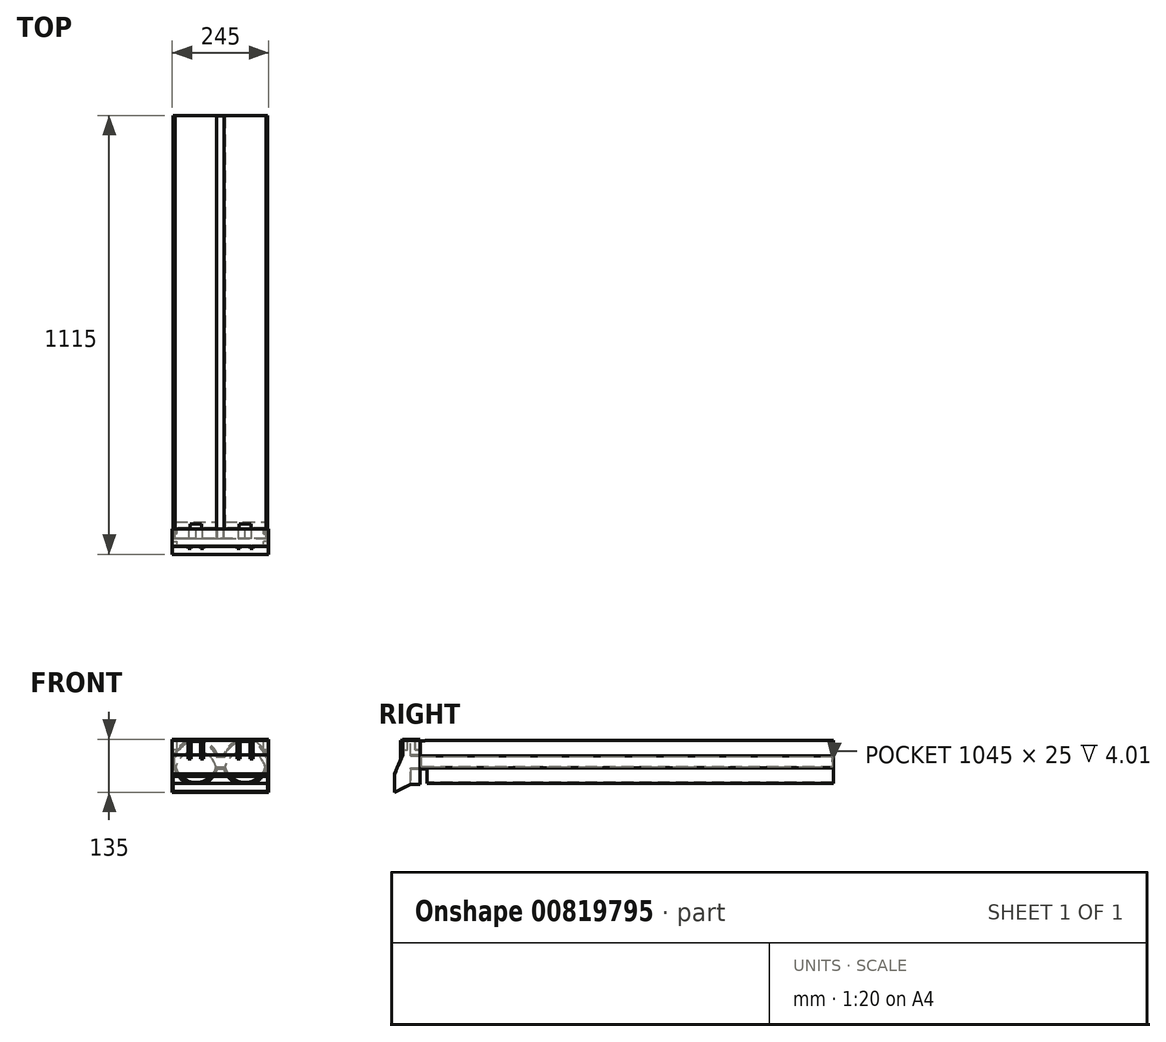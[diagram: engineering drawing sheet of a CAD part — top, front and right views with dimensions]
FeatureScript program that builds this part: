
annotation { "Feature Type Name" : "Feature", "Feature Type Description" : "" }
export const myFeature = defineFeature(function(context is Context, id is Id, definition is map)
    precondition{}
    {
        {
            var Q0;
            Q0=qCreatedBy(makeId("Front.planeOp"),FACE);
            var sketch = newSketch(context, id + "F0", { "sketchPlane" : qUnion([Q0])});
            skLineSegment(sketch, "E0.bottom", {"start": v(-9.58, 15) * mm, "end": v(9.58, 15) * mm});
            skLineSegment(sketch, "E0.top", {"start": v(-9.58, -15) * mm, "end": v(9.58, -15) * mm});
            skLineSegment(sketch, "E0.left", {"start": v(-9.58, 15) * mm, "end": v(-9.58, -15) * mm, "construction": true});
            skLineSegment(sketch, "E0.right", {"start": v(9.58, 15) * mm, "end": v(9.58, -15) * mm, "construction": true});
            skPoint(sketch, "E0.middle", {"position": v(0, 0) * mm});
            skCircle(sketch, "E1", {"center": v(-62.5, 0) * mm, "radius": 55 * mm});
            skCircle(sketch, "E2", {"center": v(62.5, 0) * mm, "radius": 55 * mm});
            skLineSegment(sketch, "E3.bottom", {"start": v(-115.42, 15) * mm, "end": v(-120, 15) * mm});
            skLineSegment(sketch, "E3.top", {"start": v(-115.42, -15) * mm, "end": v(-120, -15) * mm});
            skLineSegment(sketch, "E3.left", {"start": v(-115.42, 15) * mm, "end": v(-115.42, -15) * mm, "construction": true});
            skLineSegment(sketch, "E3.right", {"start": v(-120, 15) * mm, "end": v(-120, -15) * mm});
            skLineSegment(sketch, "E4.bottom", {"start": v(115.42, 15) * mm, "end": v(120, 15) * mm});
            skLineSegment(sketch, "E4.top", {"start": v(115.42, -15) * mm, "end": v(120, -15) * mm});
            skLineSegment(sketch, "E4.left", {"start": v(115.42, 15) * mm, "end": v(115.42, -15) * mm, "construction": true});
            skLineSegment(sketch, "E4.right", {"start": v(120, 15) * mm, "end": v(120, -15) * mm});
            skSolve(sketch);
        }
        {
            var Q0;
            {var subQ0=sQuery(id+"F0.wireOp",EDGE,"E2");var subQ1=makeQuery(id+"F0.imprint","INTERSECT",VERTEX,{"derivedFrom":[sQuery(id+"F0.wireOp",EDGE,"E0.bottom"),subQ0]});Q0=makeQuery(id+"F0.imprint","IMPRINT",FACE,{"disambiguationData":[TD([[makeQuery(id+"F0.imprint","IMPRINT",EDGE,{"disambiguationData":[TD([[subQ1,1.0]])],"derivedFrom":subQ0}),1.0]])]});}
            var Q1;
            {var subQ0=sQuery(id+"F0.wireOp",EDGE,"E4.bottom");Q1=makeQuery(id+"F0.imprint","IMPRINT",FACE,{"disambiguationData":[TD([[makeQuery(id+"F0.imprint","IMPRINT",EDGE,{"derivedFrom":subQ0}),-1.0]])]});}
            var Q2;
            {var subQ0=sQuery(id+"F0.wireOp",EDGE,"E0.bottom");Q2=makeQuery(id+"F0.imprint","IMPRINT",FACE,{"disambiguationData":[TD([[makeQuery(id+"F0.imprint","IMPRINT",EDGE,{"derivedFrom":subQ0}),-1.0]])]});}
            var Q3;
            {var subQ0=sQuery(id+"F0.wireOp",EDGE,"E1");var subQ1=makeQuery(id+"F0.imprint","INTERSECT",VERTEX,{"derivedFrom":[sQuery(id+"F0.wireOp",EDGE,"E0.bottom"),subQ0]});Q3=makeQuery(id+"F0.imprint","IMPRINT",FACE,{"disambiguationData":[TD([[makeQuery(id+"F0.imprint","IMPRINT",EDGE,{"disambiguationData":[TD([[subQ1,-1.0]])],"derivedFrom":subQ0}),1.0]])]});}
            var Q4;
            {var subQ0=sQuery(id+"F0.wireOp",EDGE,"E3.bottom");Q4=makeQuery(id+"F0.imprint","IMPRINT",FACE,{"disambiguationData":[TD([[makeQuery(id+"F0.imprint","IMPRINT",EDGE,{"derivedFrom":subQ0}),1.0]])]});}
            extrude(context, id + "F1", {"entities" : qUnion([Q0, Q1, Q2, Q3, Q4]), "oppositeDirection" : true, "depth" : 1050 * mm, "offsetDistance" : 25 * mm});
        }
        {
            var Q0;
            Q0=makeQuery(id+"F1.opExtrude","CAP_FACE",FACE,{"disambiguationData":[OSD([sQuery(id+"F0.wireOp",EDGE,"E0.bottom"),sQuery(id+"F0.wireOp",EDGE,"E0.top"),sQuery(id+"F0.wireOp",EDGE,"E1"),sQuery(id+"F0.wireOp",EDGE,"E2"),sQuery(id+"F0.wireOp",EDGE,"E3.bottom"),sQuery(id+"F0.wireOp",EDGE,"E3.top"),sQuery(id+"F0.wireOp",EDGE,"E3.right"),sQuery(id+"F0.wireOp",EDGE,"E4.bottom"),sQuery(id+"F0.wireOp",EDGE,"E4.top"),sQuery(id+"F0.wireOp",EDGE,"E4.right")])],"isStart":true});
            shell(context, id + "F2", {"entities" : qUnion([Q0]), "thickness" : 2.5 * mm});
        }
        {
            var Q0;
            Q0=qCreatedBy(makeId("Front.planeOp"),FACE);
            var sketch = newSketch(context, id + "F3", { "sketchPlane" : qUnion([Q0])});
            skLineSegment(sketch, "E5.bottom", {"start": v(122.5, -57.5) * mm, "end": v(-122.5, -57.5) * mm});
            skLineSegment(sketch, "E5.top", {"start": v(122.5, 57.5) * mm, "end": v(-122.5, 57.5) * mm});
            skLineSegment(sketch, "E5.left", {"start": v(122.5, -57.5) * mm, "end": v(122.5, 57.5) * mm});
            skLineSegment(sketch, "E5.right", {"start": v(-122.5, -57.5) * mm, "end": v(-122.5, 57.5) * mm});
            skPoint(sketch, "E5.middle", {"position": v(0, 0) * mm});
            skSolve(sketch);
        }
        {
            var Q0;
            Q0=makeQuery(id+"F3.imprint","IMPRINT",FACE,{"disambiguationData":[TD([[makeQuery(id+"F3.imprint","IMPRINT",EDGE,{"derivedFrom":sQuery(id+"F3.wireOp",EDGE,"E5.bottom")}),-1.0]])]});
            extrude(context, id + "F4", {"entities" : qUnion([Q0]), "depth" : 25 * mm, "offsetDistance" : 25 * mm});
        }
        {
            var Q0;
            {var subQ0=sQuery(id+"F0.wireOp",EDGE,"E3.bottom");Q0=makeQuery(id+"F0.imprint","IMPRINT",FACE,{"disambiguationData":[TD([[makeQuery(id+"F0.imprint","IMPRINT",EDGE,{"derivedFrom":subQ0}),1.0]])]});}
            var Q1;
            {var subQ0=sQuery(id+"F0.wireOp",EDGE,"E1");var subQ1=makeQuery(id+"F0.imprint","INTERSECT",VERTEX,{"derivedFrom":[sQuery(id+"F0.wireOp",EDGE,"E0.bottom"),subQ0]});Q1=makeQuery(id+"F0.imprint","IMPRINT",FACE,{"disambiguationData":[TD([[makeQuery(id+"F0.imprint","IMPRINT",EDGE,{"disambiguationData":[TD([[subQ1,-1.0]])],"derivedFrom":subQ0}),1.0]])]});}
            var Q2;
            {var subQ0=sQuery(id+"F0.wireOp",EDGE,"E0.bottom");Q2=makeQuery(id+"F0.imprint","IMPRINT",FACE,{"disambiguationData":[TD([[makeQuery(id+"F0.imprint","IMPRINT",EDGE,{"derivedFrom":subQ0}),-1.0]])]});}
            var Q3;
            {var subQ0=sQuery(id+"F0.wireOp",EDGE,"E2");var subQ1=makeQuery(id+"F0.imprint","INTERSECT",VERTEX,{"derivedFrom":[sQuery(id+"F0.wireOp",EDGE,"E0.bottom"),subQ0]});Q3=makeQuery(id+"F0.imprint","IMPRINT",FACE,{"disambiguationData":[TD([[makeQuery(id+"F0.imprint","IMPRINT",EDGE,{"disambiguationData":[TD([[subQ1,1.0]])],"derivedFrom":subQ0}),1.0]])]});}
            var Q4;
            {var subQ0=sQuery(id+"F0.wireOp",EDGE,"E4.bottom");Q4=makeQuery(id+"F0.imprint","IMPRINT",FACE,{"disambiguationData":[TD([[makeQuery(id+"F0.imprint","IMPRINT",EDGE,{"derivedFrom":subQ0}),-1.0]])]});}
            extrude(context, id + "F5", {"entities" : qUnion([Q0, Q1, Q2, Q3, Q4]), "operationType" : NewBodyOperationType.REMOVE, "depth" : 25 * mm, "offsetDistance" : 25 * mm});
        }
        {
            var Q0;
            Q0=makeQuery(id+"F1.opExtrude","CAP_FACE",FACE,{"disambiguationData":[OSD([sQuery(id+"F0.wireOp",EDGE,"E0.bottom"),sQuery(id+"F0.wireOp",EDGE,"E0.top"),sQuery(id+"F0.wireOp",EDGE,"E1"),sQuery(id+"F0.wireOp",EDGE,"E2"),sQuery(id+"F0.wireOp",EDGE,"E3.bottom"),sQuery(id+"F0.wireOp",EDGE,"E3.top"),sQuery(id+"F0.wireOp",EDGE,"E3.right"),sQuery(id+"F0.wireOp",EDGE,"E4.bottom"),sQuery(id+"F0.wireOp",EDGE,"E4.top"),sQuery(id+"F0.wireOp",EDGE,"E4.right")])],"isStart":true});
            var sketch = newSketch(context, id + "F6", { "sketchPlane" : qUnion([Q0])});
            skLineSegment(sketch, "E6", {"start": v(-62.5, 52.5) * mm, "end": v(-62.5, -52.5) * mm, "construction": true});
            skLineSegment(sketch, "E7", {"start": v(62.5, 52.5) * mm, "end": v(62.5, -52.5) * mm, "construction": true});
            skLineSegment(sketch, "E8", {"start": v(-120, 0) * mm, "end": v(120, 0) * mm, "construction": true});
            skCircle(sketch, "E9", {"center": v(-62.5, -25) * mm, "radius": 52.5 * mm});
            skCircle(sketch, "E10", {"center": v(62.5, -25) * mm, "radius": 52.5 * mm});
            skSolve(sketch);
        }
        {
            var Q0;
            {var subQ10=sQuery(id+"F0.wireOp",EDGE,"E0.bottom");Q0=makeQuery(id+"F6.imprint","IMPRINT",FACE,{"disambiguationData":[TD([[makeQuery(id+"F6.imprint","IMPRINT",EDGE,{"derivedFrom":makeQuery(id+"F2.opShell","OFFSET_EDGE",EDGE,{"disambiguationData":[OSD([subQ10]),TDD([makeQuery(id+"F1.opExtrude","CAP_EDGE",EDGE,{"disambiguationData":[OSD([subQ10])],"isStart":true})])]})}),-1.0]])]});}
            extrude(context, id + "F7", {"entities" : qUnion([Q0]), "operationType" : NewBodyOperationType.ADD, "oppositeDirection" : true, "depth" : 2.5 * mm, "offsetDistance" : 25 * mm});
        }
        {
            var Q0;
            {var subQ1=sQuery(id+"F0.wireOp",EDGE,"E1");var subQ2=sQuery(id+"F0.wireOp",EDGE,"E0.top");var subQ4=makeQuery(id+"F1.opExtrude","CAP_EDGE",EDGE,{"disambiguationData":[OSD([subQ1]),TDD([makeQuery(id+"F0.imprint","IMPRINT",EDGE,{"disambiguationData":[TD([[makeQuery(id+"F0.imprint","INTERSECT",VERTEX,{"derivedFrom":[subQ2,subQ1]}),1.0]])],"derivedFrom":subQ1})])],"isStart":true});var subQ5=makeQuery(id+"F2.opShell","OFFSET_EDGE",EDGE,{"disambiguationData":[OSD([subQ1]),TDD([subQ4])]});Q0=makeQuery(id+"F6.imprint","IMPRINT",FACE,{"disambiguationData":[TD([[makeQuery(id+"F6.imprint","IMPRINT",EDGE,{"derivedFrom":subQ5}),-1.0]])]});}
            var Q1;
            {var subQ2=sQuery(id+"F0.wireOp",EDGE,"E2");var subQ3=sQuery(id+"F0.wireOp",EDGE,"E0.top");var subQ4=makeQuery(id+"F1.opExtrude","CAP_EDGE",EDGE,{"disambiguationData":[OSD([subQ2]),TDD([makeQuery(id+"F0.imprint","IMPRINT",EDGE,{"disambiguationData":[TD([[makeQuery(id+"F0.imprint","INTERSECT",VERTEX,{"derivedFrom":[subQ3,subQ2]}),-1.0]])],"derivedFrom":subQ2})])],"isStart":true});var subQ5=makeQuery(id+"F2.opShell","OFFSET_EDGE",EDGE,{"disambiguationData":[OSD([subQ2]),TDD([subQ4])]});Q1=makeQuery(id+"F6.imprint","IMPRINT",FACE,{"disambiguationData":[TD([[makeQuery(id+"F6.imprint","IMPRINT",EDGE,{"derivedFrom":subQ5}),-1.0]])]});}
            extrude(context, id + "F8", {"entities" : qUnion([Q0, Q1]), "operationType" : NewBodyOperationType.REMOVE, "oppositeDirection" : true, "depth" : 17.5 * mm, "offsetDistance" : 25 * mm});
        }
        {
            var Q0;
            {var subQ0=sQuery(id+"F0.wireOp",EDGE,"E4.right");var subQ1=sQuery(id+"F0.wireOp",EDGE,"E4.top");var subQ2=sQuery(id+"F0.wireOp",EDGE,"E4.bottom");var subQ3=sQuery(id+"F0.wireOp",EDGE,"E3.right");var subQ4=sQuery(id+"F0.wireOp",EDGE,"E3.top");var subQ5=sQuery(id+"F0.wireOp",EDGE,"E3.bottom");var subQ6=sQuery(id+"F0.wireOp",EDGE,"E2");var subQ7=sQuery(id+"F0.wireOp",EDGE,"E1");var subQ8=sQuery(id+"F0.wireOp",EDGE,"E0.top");var subQ9=sQuery(id+"F0.wireOp",EDGE,"E0.bottom");Q0=makeQuery(id+"F7.boolean.opBoolean","MERGE",FACE,{"derivedFrom":[makeQuery(id+"F1.opExtrude","CAP_FACE",FACE,{"disambiguationData":[OSD([subQ9,subQ8,subQ7,subQ6,subQ5,subQ4,subQ3,subQ2,subQ1,subQ0])],"isStart":true}),makeQuery(id+"F7.opExtrude","CAP_FACE",FACE,{"disambiguationData":[OSD([subQ9,subQ8,subQ7,subQ6,subQ5,subQ4,subQ3,subQ2,subQ1,subQ0,sQuery(id+"F6.wireOp",EDGE,"E9"),sQuery(id+"F6.wireOp",EDGE,"E10")])],"isStart":true})]});}
            var sketch = newSketch(context, id + "F9", { "sketchPlane" : qUnion([Q0])});
            skLineSegment(sketch, "E11", {"start": v(-62.5, 55) * mm, "end": v(-62.5, -55.98) * mm, "construction": true});
            skLineSegment(sketch, "E12", {"start": v(62.5, 55) * mm, "end": v(62.5, -55.98) * mm, "construction": true});
            skLineSegment(sketch, "E13", {"start": v(-77.5, 52.92) * mm, "end": v(-77.5, 25.31) * mm});
            skLineSegment(sketch, "E14", {"start": v(-47.5, 52.92) * mm, "end": v(-47.5, 25.31) * mm});
            skLineSegment(sketch, "E15", {"start": v(47.5, 52.92) * mm, "end": v(47.5, 25.31) * mm});
            skLineSegment(sketch, "E16", {"start": v(77.5, 52.92) * mm, "end": v(77.5, 25.31) * mm});
            skSolve(sketch);
        }
        {
            var Q0;
            {var subQ0=sQuery(id+"F9.wireOp",EDGE,"E13");Q0=makeQuery(id+"F9.imprint","IMPRINT",FACE,{"disambiguationData":[TD([[makeQuery(id+"F9.imprint","IMPRINT",EDGE,{"derivedFrom":subQ0}),1.0]])]});}
            var Q1;
            {var subQ0=sQuery(id+"F9.wireOp",EDGE,"E15");Q1=makeQuery(id+"F9.imprint","IMPRINT",FACE,{"disambiguationData":[TD([[makeQuery(id+"F9.imprint","IMPRINT",EDGE,{"derivedFrom":subQ0}),1.0]])]});}
            extrude(context, id + "F10", {"entities" : qUnion([Q0, Q1]), "operationType" : NewBodyOperationType.REMOVE, "oppositeDirection" : true, "depth" : 12.5 * mm, "offsetDistance" : 25 * mm});
        }
        {
            var Q0;
            Q0=makeQuery(id+"F4.opExtrude","SWEPT_FACE",FACE,{"disambiguationData":[OSD([sQuery(id+"F3.wireOp",EDGE,"E5.right")])]});
            var sketch = newSketch(context, id + "F11", { "sketchPlane" : qUnion([Q0])});
            skLineSegment(sketch, "E17", {"start": v(25, 57.5) * mm, "end": v(45, 57.5) * mm});
            skLineSegment(sketch, "E18", {"start": v(45, 57.5) * mm, "end": v(45, 17.5) * mm});
            skLineSegment(sketch, "E19", {"start": v(45, 17.5) * mm, "end": v(85, -77.5) * mm});
            skLineSegment(sketch, "E20", {"start": v(85, -77.5) * mm, "end": v(65, -77.5) * mm});
            skLineSegment(sketch, "E21", {"start": v(65, -77.5) * mm, "end": v(25, -57.5) * mm});
            skLineSegment(sketch, "E22", {"start": v(65, -77.5) * mm, "end": v(65, -30) * mm});
            skSolve(sketch);
        }
        {
            var Q0;
            Q0=makeQuery(id+"F11.imprint","IMPRINT",FACE,{"disambiguationData":[TD([[makeQuery(id+"F11.imprint","IMPRINT",EDGE,{"derivedFrom":sQuery(id+"F11.wireOp",EDGE,"E17")}),-1.0]])]});
            extrude(context, id + "F12", {"entities" : qUnion([Q0]), "operationType" : NewBodyOperationType.ADD, "oppositeDirection" : true, "depth" : 245 * mm, "offsetDistance" : 25 * mm});
        }
        {
            var Q0;
            Q0=makeQuery(id+"F12.opExtrude","SWEPT_FACE",FACE,{"disambiguationData":[OSD([sQuery(id+"F11.wireOp",EDGE,"E22")])]});
            var Q1;
            Q1=makeQuery(id+"F12.opExtrude","SWEPT_FACE",FACE,{"disambiguationData":[OSD([sQuery(id+"F3.wireOp",EDGE,"E5.right")])]});
            shell(context, id + "F13", {"entities" : qUnion([Q0, Q1]), "thickness" : 2.5 * mm});
        }
        {
            var Q0;
            Q0=makeQuery(id+"F12.opExtrude","SWEPT_FACE",FACE,{"disambiguationData":[OSD([sQuery(id+"F11.wireOp",EDGE,"E18")])]});
            var sketch = newSketch(context, id + "F14", { "sketchPlane" : qUnion([Q0])});
            skLineSegment(sketch, "E23.bottom", {"start": v(-77.5, 57.5) * mm, "end": v(-47.5, 57.5) * mm});
            skLineSegment(sketch, "E23.top", {"start": v(-77.5, 7.5) * mm, "end": v(-47.5, 7.5) * mm});
            skLineSegment(sketch, "E23.left", {"start": v(-77.5, 57.5) * mm, "end": v(-77.5, 7.5) * mm});
            skLineSegment(sketch, "E23.right", {"start": v(-47.5, 57.5) * mm, "end": v(-47.5, 7.5) * mm});
            skLineSegment(sketch, "E24.bottom", {"start": v(47.5, 57.5) * mm, "end": v(77.5, 57.5) * mm});
            skLineSegment(sketch, "E24.top", {"start": v(47.5, 7.5) * mm, "end": v(77.5, 7.5) * mm});
            skLineSegment(sketch, "E24.left", {"start": v(47.5, 57.5) * mm, "end": v(47.5, 7.5) * mm});
            skLineSegment(sketch, "E24.right", {"start": v(77.5, 57.5) * mm, "end": v(77.5, 7.5) * mm});
            skLineSegment(sketch, "E25", {"start": v(-62.5, 57.5) * mm, "end": v(-62.5, 17.5) * mm, "construction": true});
            skLineSegment(sketch, "E26", {"start": v(62.5, 57.5) * mm, "end": v(62.5, 0) * mm, "construction": true});
            skSolve(sketch);
        }
        {
            var Q0;
            Q0=makeQuery(id+"F14.imprint","IMPRINT",FACE,{"disambiguationData":[TD([[makeQuery(id+"F14.imprint","IMPRINT",EDGE,{"derivedFrom":sQuery(id+"F14.wireOp",EDGE,"E23.bottom")}),1.0]])]});
            var Q1;
            Q1=makeQuery(id+"F14.imprint","IMPRINT",FACE,{"disambiguationData":[TD([[makeQuery(id+"F14.imprint","IMPRINT",EDGE,{"derivedFrom":sQuery(id+"F14.wireOp",EDGE,"E24.bottom")}),1.0]])]});
            extrude(context, id + "F15", {"entities" : qUnion([Q0, Q1]), "operationType" : NewBodyOperationType.REMOVE, "oppositeDirection" : true, "depth" : 2.5 * mm, "offsetDistance" : 25 * mm});
        }
        {
            var Q0;
            Q0=makeQuery(id+"F12.boolean.opBoolean","MERGE",FACE,{"derivedFrom":[makeQuery(id+"F4.opExtrude","SWEPT_FACE",FACE,{"disambiguationData":[OSD([sQuery(id+"F3.wireOp",EDGE,"E5.top")])]}),makeQuery(id+"F12.opExtrude","SWEPT_FACE",FACE,{"disambiguationData":[OSD([sQuery(id+"F11.wireOp",EDGE,"E17")])]})]});
            var sketch = newSketch(context, id + "F16", { "sketchPlane" : qUnion([Q0])});
            skLineSegment(sketch, "E27.bottom", {"start": v(-82.5, -45) * mm, "end": v(-80, -45) * mm});
            skLineSegment(sketch, "E27.top", {"start": v(-82.5, -47.5) * mm, "end": v(-80, -47.5) * mm});
            skLineSegment(sketch, "E27.left", {"start": v(-82.5, -45) * mm, "end": v(-82.5, -47.5) * mm});
            skLineSegment(sketch, "E27.right", {"start": v(-80, -45) * mm, "end": v(-80, -47.5) * mm});
            skLineSegment(sketch, "E28.bottom", {"start": v(-82.5, -47.5) * mm, "end": v(-75, -47.5) * mm});
            skLineSegment(sketch, "E28.top", {"start": v(-82.5, -50) * mm, "end": v(-75, -50) * mm});
            skLineSegment(sketch, "E28.left", {"start": v(-82.5, -47.5) * mm, "end": v(-82.5, -50) * mm});
            skLineSegment(sketch, "E28.right", {"start": v(-75, -47.5) * mm, "end": v(-75, -50) * mm});
            skLineSegment(sketch, "E29", {"start": v(-62.5, -42.5) * mm, "end": v(-62.5, -62.36) * mm, "construction": true});
            skLineSegment(sketch, "E30.MirrorCS", {"start": v(-50, -47.5) * mm, "end": v(-50, -50) * mm});
            skLineSegment(sketch, "E31.MirrorCS", {"start": v(-42.5, -47.5) * mm, "end": v(-50, -47.5) * mm});
            skLineSegment(sketch, "E32.MirrorCS", {"start": v(-42.5, -50) * mm, "end": v(-50, -50) * mm});
            skLineSegment(sketch, "E33.MirrorCS", {"start": v(-42.5, -47.5) * mm, "end": v(-42.5, -50) * mm});
            skLineSegment(sketch, "E34.MirrorCS", {"start": v(-42.5, -45) * mm, "end": v(-42.5, -47.5) * mm});
            skLineSegment(sketch, "E35.MirrorCS", {"start": v(-45, -45) * mm, "end": v(-45, -47.5) * mm});
            skLineSegment(sketch, "E36.MirrorCS", {"start": v(-42.5, -45) * mm, "end": v(-45, -45) * mm});
            skLineSegment(sketch, "E37", {"start": v(0, -7.26) * mm, "end": v(0, -62.51) * mm, "construction": true});
            skPoint(sketch, "E37.endSnap0", {"position": v(0, -45) * mm});
            skLineSegment(sketch, "E38.MirrorCS", {"start": v(42.5, -45) * mm, "end": v(42.5, -47.5) * mm});
            skLineSegment(sketch, "E39.MirrorCS", {"start": v(42.5, -45) * mm, "end": v(45, -45) * mm});
            skLineSegment(sketch, "E40.MirrorCS", {"start": v(45, -45) * mm, "end": v(45, -47.5) * mm});
            skLineSegment(sketch, "E41.MirrorCS", {"start": v(42.5, -47.5) * mm, "end": v(50, -47.5) * mm});
            skLineSegment(sketch, "E42.MirrorCS", {"start": v(42.5, -47.5) * mm, "end": v(42.5, -50) * mm});
            skLineSegment(sketch, "E43.MirrorCS", {"start": v(42.5, -50) * mm, "end": v(50, -50) * mm});
            skLineSegment(sketch, "E44.MirrorCS", {"start": v(50, -47.5) * mm, "end": v(50, -50) * mm});
            skLineSegment(sketch, "E45.MirrorCS", {"start": v(82.5, -45) * mm, "end": v(80, -45) * mm});
            skLineSegment(sketch, "E46.MirrorCS", {"start": v(82.5, -45) * mm, "end": v(82.5, -47.5) * mm});
            skLineSegment(sketch, "E47.MirrorCS", {"start": v(80, -45) * mm, "end": v(80, -47.5) * mm});
            skLineSegment(sketch, "E48.MirrorCS", {"start": v(82.5, -47.5) * mm, "end": v(75, -47.5) * mm});
            skLineSegment(sketch, "E49.MirrorCS", {"start": v(82.5, -47.5) * mm, "end": v(82.5, -50) * mm});
            skLineSegment(sketch, "E50.MirrorCS", {"start": v(82.5, -50) * mm, "end": v(75, -50) * mm});
            skLineSegment(sketch, "E51.MirrorCS", {"start": v(75, -47.5) * mm, "end": v(75, -50) * mm});
            skSolve(sketch);
        }
        {
            var Q0;
            Q0=makeQuery(id+"F16.imprint","IMPRINT",FACE,{"disambiguationData":[TD([[makeQuery(id+"F16.imprint","IMPRINT",EDGE,{"derivedFrom":sQuery(id+"F16.wireOp",EDGE,"E27.bottom")}),1.0]])]});
            var Q1;
            Q1=makeQuery(id+"F16.imprint","IMPRINT",FACE,{"disambiguationData":[TD([[makeQuery(id+"F16.imprint","IMPRINT",EDGE,{"derivedFrom":sQuery(id+"F16.wireOp",EDGE,"E28.top")}),1.0]])]});
            var Q2;
            {var subQ0=sQuery(id+"F16.wireOp",EDGE,"E34.MirrorCS");Q2=makeQuery(id+"F16.imprint","IMPRINT",FACE,{"disambiguationData":[TD([[makeQuery(id+"F16.imprint","IMPRINT",EDGE,{"derivedFrom":subQ0}),-1.0]])]});}
            var Q3;
            {var subQ1=sQuery(id+"F16.wireOp",EDGE,"E30.MirrorCS");Q3=makeQuery(id+"F16.imprint","IMPRINT",FACE,{"disambiguationData":[TD([[makeQuery(id+"F16.imprint","IMPRINT",EDGE,{"derivedFrom":subQ1}),1.0]])]});}
            var Q4;
            {var subQ0=sQuery(id+"F16.wireOp",EDGE,"E42.MirrorCS");Q4=makeQuery(id+"F16.imprint","IMPRINT",FACE,{"disambiguationData":[TD([[makeQuery(id+"F16.imprint","IMPRINT",EDGE,{"derivedFrom":subQ0}),1.0]])]});}
            var Q5;
            {var subQ0=sQuery(id+"F16.wireOp",EDGE,"E38.MirrorCS");Q5=makeQuery(id+"F16.imprint","IMPRINT",FACE,{"disambiguationData":[TD([[makeQuery(id+"F16.imprint","IMPRINT",EDGE,{"derivedFrom":subQ0}),1.0]])]});}
            var Q6;
            {var subQ0=sQuery(id+"F16.wireOp",EDGE,"E49.MirrorCS");Q6=makeQuery(id+"F16.imprint","IMPRINT",FACE,{"disambiguationData":[TD([[makeQuery(id+"F16.imprint","IMPRINT",EDGE,{"derivedFrom":subQ0}),-1.0]])]});}
            var Q7;
            Q7=makeQuery(id+"F16.imprint","IMPRINT",FACE,{"disambiguationData":[TD([[makeQuery(id+"F16.imprint","IMPRINT",EDGE,{"derivedFrom":sQuery(id+"F16.wireOp",EDGE,"E45.MirrorCS")}),1.0]])]});
            extrude(context, id + "F17", {"entities" : qUnion([Q0, Q1, Q2, Q3, Q4, Q5, Q6, Q7]), "operationType" : NewBodyOperationType.ADD, "oppositeDirection" : true, "depth" : 50 * mm, "offsetDistance" : 25 * mm});
        }
        {
            var Q0;
            Q0=makeQuery(id+"F17.opExtrude","SWEPT_FACE",FACE,{"disambiguationData":[OSD([sQuery(id+"F16.wireOp",EDGE,"E28.top")])]});
            var sketch = newSketch(context, id + "F18", { "sketchPlane" : qUnion([Q0])});
            skLineSegment(sketch, "E52.bottom", {"start": v(-122.5, 57.5) * mm, "end": v(122.5, 57.5) * mm});
            skLineSegment(sketch, "E52.top", {"start": v(-122.5, 55) * mm, "end": v(122.5, 55) * mm});
            skLineSegment(sketch, "E52.left", {"start": v(-122.5, 57.5) * mm, "end": v(-122.5, 55) * mm});
            skLineSegment(sketch, "E52.right", {"start": v(122.5, 57.5) * mm, "end": v(122.5, 55) * mm});
            skSolve(sketch);
        }
        {
            var Q0;
            {var subQ3=sQuery(id+"F18.wireOp",EDGE,"E52.left");Q0=makeQuery(id+"F18.imprint","IMPRINT",FACE,{"disambiguationData":[TD([[makeQuery(id+"F18.imprint","IMPRINT",EDGE,{"derivedFrom":subQ3}),1.0]])]});}
            var Q1;
            {var subQ0=sQuery(id+"F18.wireOp",EDGE,"E52.bottom");var subQ1=sQuery(id+"F16.wireOp",EDGE,"E28.top");var subQ2=makeQuery(id+"F17.opExtrude","SWEPT_EDGE",EDGE,{"disambiguationData":[OSD([subQ1,sQuery(id+"F16.wireOp",EDGE,"E28.left")])]});var subQ3=makeQuery(id+"F18.imprint","INTERSECT",VERTEX,{"derivedFrom":[subQ2,subQ0]});Q1=makeQuery(id+"F18.imprint","IMPRINT",FACE,{"disambiguationData":[TD([[makeQuery(id+"F18.imprint","IMPRINT",EDGE,{"disambiguationData":[TD([[subQ3,-1.0]])],"derivedFrom":subQ0}),-1.0]])]});}
            var Q2;
            {var subQ3=sQuery(id+"F18.wireOp",EDGE,"E52.right");Q2=makeQuery(id+"F18.imprint","IMPRINT",FACE,{"disambiguationData":[TD([[makeQuery(id+"F18.imprint","IMPRINT",EDGE,{"derivedFrom":subQ3}),-1.0]])]});}
            extrude(context, id + "F19", {"entities" : qUnion([Q0, Q1, Q2]), "operationType" : NewBodyOperationType.REMOVE, "oppositeDirection" : true, "depth" : 50 * mm, "offsetDistance" : 25 * mm});
        }
        {
            var Q0;
            {var subQ0=sQuery(id+"F3.wireOp",EDGE,"E5.right");Q0=makeQuery(id+"F19.boolean.opBoolean","COPY",FACE,{"disambiguationData":[TD([makeQuery(id+"F4.opExtrude","SWEPT_FACE",FACE,{"disambiguationData":[OSD([subQ0])]})])],"derivedFrom":makeQuery(id+"F19.opExtrude","SWEPT_FACE",FACE,{"disambiguationData":[OSD([sQuery(id+"F18.wireOp",EDGE,"E52.top")])]})});}
            var sketch = newSketch(context, id + "F20", { "sketchPlane" : qUnion([Q0])});
            skLineSegment(sketch, "E53.bottom", {"start": v(-120, -2.5) * mm, "end": v(-110, -2.5) * mm});
            skLineSegment(sketch, "E53.top", {"start": v(-120, -12.5) * mm, "end": v(-110, -12.5) * mm});
            skLineSegment(sketch, "E53.left", {"start": v(-120, -2.5) * mm, "end": v(-120, -12.5) * mm});
            skLineSegment(sketch, "E53.right", {"start": v(-110, -2.5) * mm, "end": v(-110, -12.5) * mm});
            skLineSegment(sketch, "E54.bottom", {"start": v(-120, -42.5) * mm, "end": v(-110, -42.5) * mm});
            skLineSegment(sketch, "E54.top", {"start": v(-120, -32.5) * mm, "end": v(-110, -32.5) * mm});
            skLineSegment(sketch, "E54.left", {"start": v(-120, -42.5) * mm, "end": v(-120, -32.5) * mm});
            skLineSegment(sketch, "E54.right", {"start": v(-110, -42.5) * mm, "end": v(-110, -32.5) * mm});
            skPoint(sketch, "E55.firstSnap0", {"position": v(-79.27, -13.75) * mm});
            skLineSegment(sketch, "E55.bottom", {"start": v(110, -13.75) * mm, "end": v(120, -13.75) * mm});
            skLineSegment(sketch, "E55.top", {"start": v(110, -2.5) * mm, "end": v(120, -2.5) * mm});
            skLineSegment(sketch, "E55.left", {"start": v(110, -13.75) * mm, "end": v(110, -2.5) * mm});
            skLineSegment(sketch, "E55.right", {"start": v(120, -13.75) * mm, "end": v(120, -2.5) * mm});
            skLineSegment(sketch, "E56.bottom", {"start": v(120, -42.5) * mm, "end": v(110, -42.5) * mm});
            skLineSegment(sketch, "E56.top", {"start": v(120, -32.5) * mm, "end": v(110, -32.5) * mm});
            skLineSegment(sketch, "E56.left", {"start": v(120, -42.5) * mm, "end": v(120, -32.5) * mm});
            skLineSegment(sketch, "E56.right", {"start": v(110, -42.5) * mm, "end": v(110, -32.5) * mm});
            skSolve(sketch);
        }
        {
            var Q0;
            Q0=makeQuery(id+"F20.imprint","IMPRINT",FACE,{"disambiguationData":[TD([[makeQuery(id+"F20.imprint","IMPRINT",EDGE,{"derivedFrom":sQuery(id+"F20.wireOp",EDGE,"E54.bottom")}),-1.0]])]});
            var Q1;
            Q1=makeQuery(id+"F20.imprint","IMPRINT",FACE,{"disambiguationData":[TD([[makeQuery(id+"F20.imprint","IMPRINT",EDGE,{"derivedFrom":sQuery(id+"F20.wireOp",EDGE,"E53.bottom")}),1.0]])]});
            var Q2;
            Q2=makeQuery(id+"F20.imprint","IMPRINT",FACE,{"disambiguationData":[TD([[makeQuery(id+"F20.imprint","IMPRINT",EDGE,{"derivedFrom":sQuery(id+"F20.wireOp",EDGE,"E56.bottom")}),-1.0]])]});
            var Q3;
            Q3=makeQuery(id+"F20.imprint","IMPRINT",FACE,{"disambiguationData":[TD([[makeQuery(id+"F20.imprint","IMPRINT",EDGE,{"derivedFrom":sQuery(id+"F20.wireOp",EDGE,"E55.bottom")}),1.0]])]});
            extrude(context, id + "F21", {"entities" : qUnion([Q0, Q1, Q2, Q3]), "operationType" : NewBodyOperationType.ADD, "oppositeDirection" : true, "depth" : 25 * mm, "offsetDistance" : 25 * mm});
        }
        {
            var Q0;
            {var subQ0=sQuery(id+"F3.wireOp",EDGE,"E5.right");Q0=makeQuery(id+"F21.boolean.opBoolean","MERGE",FACE,{"derivedFrom":[makeQuery(id+"F19.boolean.opBoolean","COPY",FACE,{"disambiguationData":[TD([makeQuery(id+"F4.opExtrude","SWEPT_FACE",FACE,{"disambiguationData":[OSD([subQ0])]})])],"derivedFrom":makeQuery(id+"F19.opExtrude","SWEPT_FACE",FACE,{"disambiguationData":[OSD([sQuery(id+"F18.wireOp",EDGE,"E52.top")])]})}),makeQuery(id+"F21.opExtrude","CAP_FACE",FACE,{"disambiguationData":[OSD([sQuery(id+"F20.wireOp",EDGE,"E53.bottom"),sQuery(id+"F20.wireOp",EDGE,"E53.top"),sQuery(id+"F20.wireOp",EDGE,"E53.left"),sQuery(id+"F20.wireOp",EDGE,"E53.right")])],"isStart":true}),makeQuery(id+"F21.opExtrude","CAP_FACE",FACE,{"disambiguationData":[OSD([sQuery(id+"F20.wireOp",EDGE,"E54.bottom"),sQuery(id+"F20.wireOp",EDGE,"E54.top"),sQuery(id+"F20.wireOp",EDGE,"E54.left"),sQuery(id+"F20.wireOp",EDGE,"E54.right")])],"isStart":true})]});}
            var sketch = newSketch(context, id + "F22", { "sketchPlane" : qUnion([Q0])});
            skLineSegment(sketch, "E57.bottom", {"start": v(-122.5, 0) * mm, "end": v(122.5, 0) * mm});
            skLineSegment(sketch, "E57.top", {"start": v(-122.5, -45) * mm, "end": v(122.5, -45) * mm});
            skLineSegment(sketch, "E57.left", {"start": v(-122.5, 0) * mm, "end": v(-122.5, -45) * mm});
            skLineSegment(sketch, "E57.right", {"start": v(122.5, 0) * mm, "end": v(122.5, -45) * mm});
            skSolve(sketch);
        }
        {
            var Q0;
            {var subQ12=sQuery(id+"F22.wireOp",EDGE,"E57.right");Q0=makeQuery(id+"F22.imprint","IMPRINT",FACE,{"disambiguationData":[TD([[makeQuery(id+"F22.imprint","IMPRINT",EDGE,{"derivedFrom":subQ12}),-1.0]])]});}
            var Q1;
            {var subQ12=sQuery(id+"F22.wireOp",EDGE,"E57.left");Q1=makeQuery(id+"F22.imprint","IMPRINT",FACE,{"disambiguationData":[TD([[makeQuery(id+"F22.imprint","IMPRINT",EDGE,{"derivedFrom":subQ12}),1.0]])]});}
            extrude(context, id + "F23", {"entities" : qUnion([Q0, Q1]), "depth" : 2.5 * mm, "offsetDistance" : 25 * mm});
        }
    });
